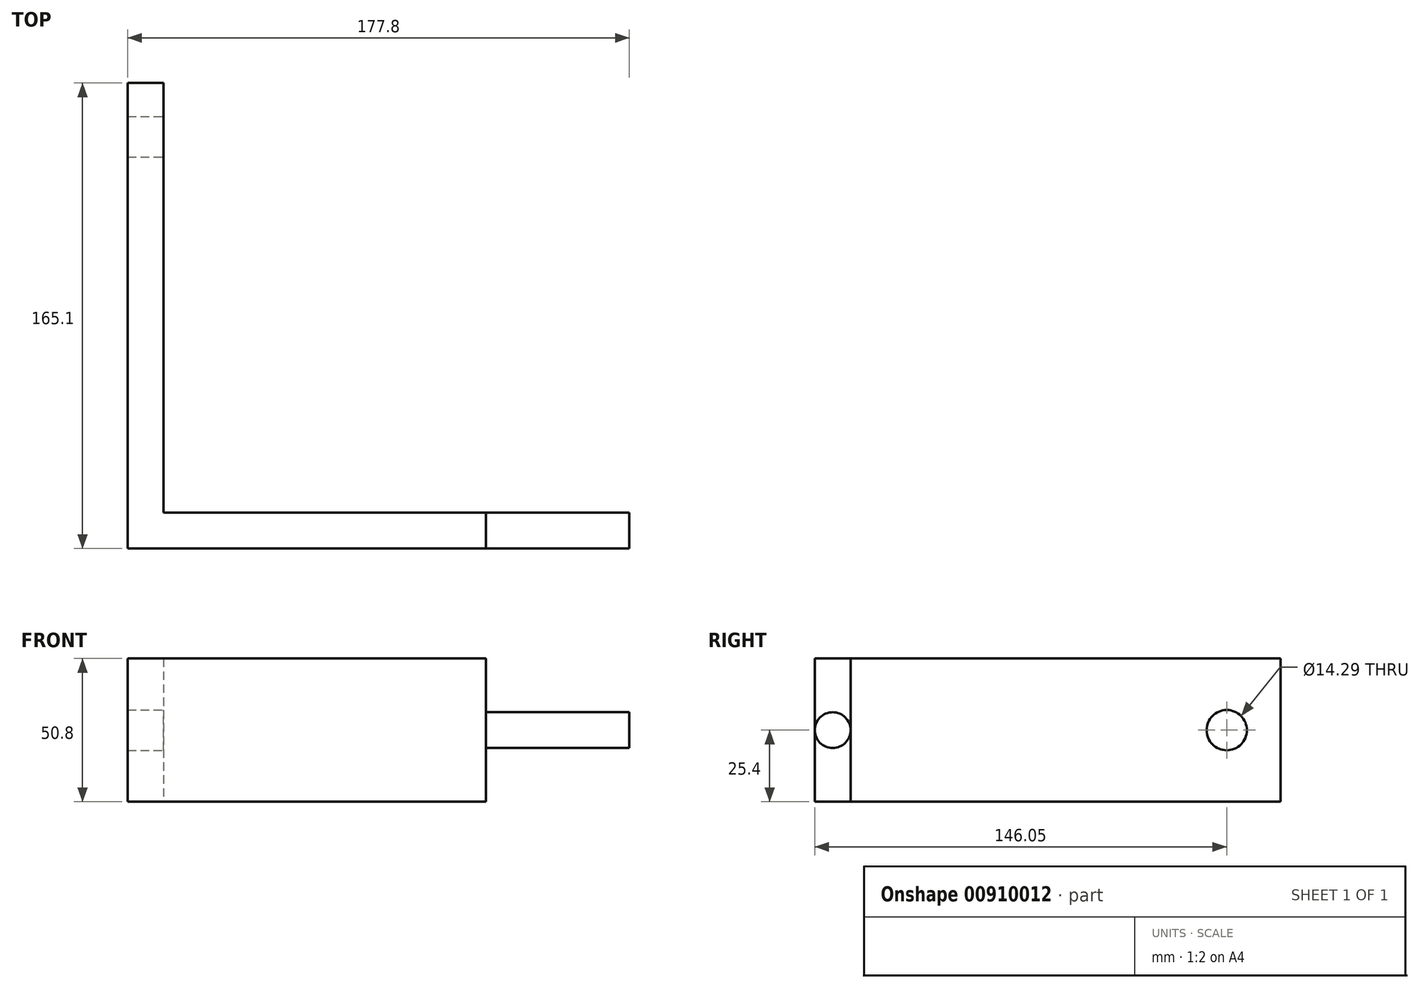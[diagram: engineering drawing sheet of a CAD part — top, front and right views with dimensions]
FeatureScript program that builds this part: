
annotation { "Feature Type Name" : "Feature", "Feature Type Description" : "" }
export const myFeature = defineFeature(function(context is Context, id is Id, definition is map)
    precondition{}
    {
        {
            var Q0;
            Q0=qCreatedBy(makeId("Top.planeOp"),FACE);
            var sketch = newSketch(context, id + "F0", { "sketchPlane" : qUnion([Q0])});
            skLineSegment(sketch, "E0.bottom", {"start": v(-76.2, 88.9) * mm, "end": v(-63.5, 88.9) * mm});
            skLineSegment(sketch, "E0.left", {"start": v(-76.2, 88.9) * mm, "end": v(-76.2, -76.2) * mm});
            skLineSegment(sketch, "E0.right", {"start": v(-63.5, 88.9) * mm, "end": v(-63.5, -63.5) * mm});
            skLineSegment(sketch, "E1.bottom", {"start": v(-63.5, -63.5) * mm, "end": v(50.8, -63.5) * mm});
            skLineSegment(sketch, "E1.top", {"start": v(-76.2, -76.2) * mm, "end": v(50.8, -76.2) * mm});
            skLineSegment(sketch, "E1.right", {"start": v(50.8, -63.5) * mm, "end": v(50.8, -76.2) * mm});
            skSolve(sketch);
        }
        {
            var Q0;
            Q0=makeQuery(id+"F0.imprint","IMPRINT",FACE,{"disambiguationData":[TD([[makeQuery(id+"F0.imprint","IMPRINT",EDGE,{"derivedFrom":sQuery(id+"F0.wireOp",EDGE,"E0.bottom")}),-1.0]])]});
            extrude(context, id + "F1", {"entities" : qUnion([Q0]), "depth" : 50.8 * mm, "offsetDistance" : 25 * mm, "symmetric" : true});
        }
        {
            var Q0;
            Q0=qCreatedBy(makeId("Right.planeOp"),FACE);
            var sketch = newSketch(context, id + "F2", { "sketchPlane" : qUnion([Q0])});
            skCircle(sketch, "E2", {"center": v(69.85, 0) * mm, "radius": 7.14 * mm});
            skSolve(sketch);
        }
        {
            var Q0;
            Q0=makeQuery(id+"F2.imprint","IMPRINT",FACE,{"disambiguationData":[TD([[makeQuery(id+"F2.imprint","IMPRINT",EDGE,{"derivedFrom":sQuery(id+"F2.wireOp",EDGE,"E2")}),1.0]])]});
            extrude(context, id + "F3", {"entities" : qUnion([Q0]), "operationType" : NewBodyOperationType.REMOVE, "endBound" : BoundingType.THROUGH_ALL, "oppositeDirection" : true, "depth" : 25 * mm, "offsetDistance" : 25 * mm});
        }
        {
            var Q0;
            Q0=makeQuery(id+"F1.opExtrude","SWEPT_FACE",FACE,{"disambiguationData":[OSD([sQuery(id+"F0.wireOp",EDGE,"E1.right")])]});
            var sketch = newSketch(context, id + "F4", { "sketchPlane" : qUnion([Q0])});
            skCircle(sketch, "E3", {"center": v(-69.85, 0) * mm, "radius": 6.35 * mm});
            skLineSegment(sketch, "E4", {"start": v(-69.85, 25.4) * mm, "end": v(-69.85, 0) * mm, "construction": true});
            skSolve(sketch);
        }
        {
            var Q0;
            {var subQ0=sQuery(id+"F4.wireOp",EDGE,"E3");var subQ1=sQuery(id+"F0.wireOp",EDGE,"E1.right");var subQ2=makeQuery(id+"F4.imprint","INTERSECT",VERTEX,{"derivedFrom":[makeQuery(id+"F1.opExtrude","SWEPT_EDGE",EDGE,{"disambiguationData":[OSD([sQuery(id+"F0.wireOp",EDGE,"E1.bottom"),subQ1])]}),subQ0]});Q0=makeQuery(id+"F4.imprint","IMPRINT",FACE,{"disambiguationData":[TD([[makeQuery(id+"F4.imprint","IMPRINT",EDGE,{"disambiguationData":[TD([[subQ2,-1.0]])],"derivedFrom":subQ0}),1.0]])]});}
            extrude(context, id + "F5", {"entities" : qUnion([Q0]), "operationType" : NewBodyOperationType.ADD, "depth" : 50.8 * mm, "offsetDistance" : 25 * mm});
        }
    });
